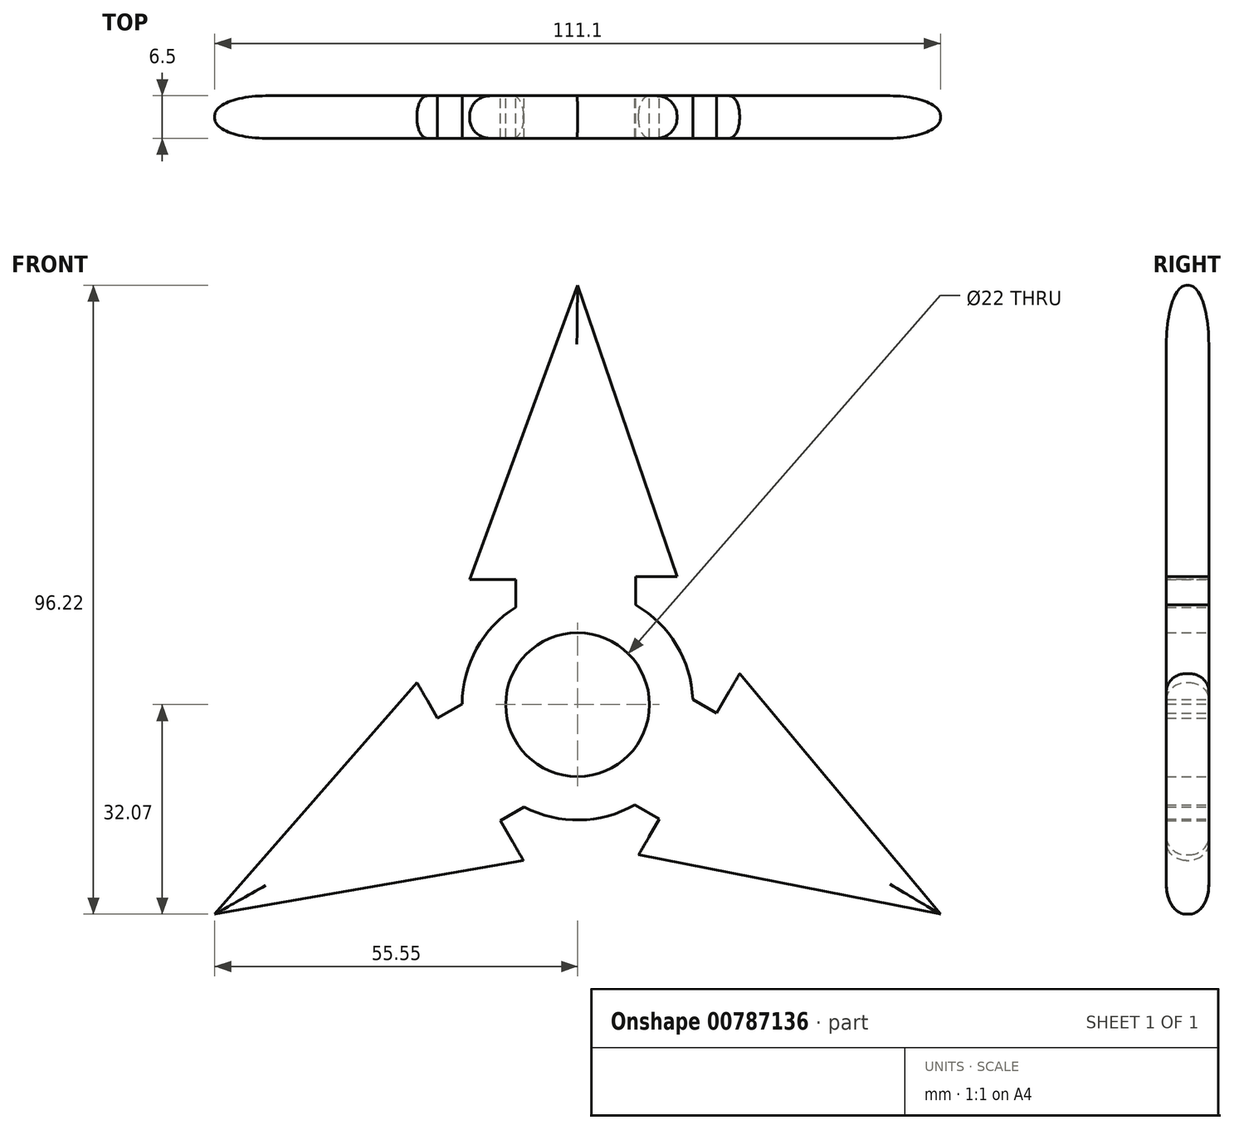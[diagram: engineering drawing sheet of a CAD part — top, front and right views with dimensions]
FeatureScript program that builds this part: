
annotation { "Feature Type Name" : "Feature", "Feature Type Description" : "" }
export const myFeature = defineFeature(function(context is Context, id is Id, definition is map)
    precondition{}
    {
        {
            var Q0;
            Q0=qCreatedBy(makeId("Front.planeOp"),FACE);
            var sketch = newSketch(context, id + "F0", { "sketchPlane" : qUnion([Q0])});
            skCircle(sketch, "E0", {"center": v(0, 0) * mm, "radius": 11 * mm});
            skCircle(sketch, "E1", {"center": v(0, 0) * mm, "radius": 17.66 * mm});
            skLineSegment(sketch, "E2", {"start": v(-16.51, 19.11) * mm, "end": v(0, 64.15) * mm});
            skLineSegment(sketch, "E3", {"start": v(0, 64.15) * mm, "end": v(15.22, 19.6) * mm});
            skLineSegment(sketch, "E4", {"start": v(8.92, 19.6) * mm, "end": v(15.22, 19.6) * mm});
            skLineSegment(sketch, "E5", {"start": v(-16.51, 19.11) * mm, "end": v(-9.49, 19.11) * mm});
            skLineSegment(sketch, "E6", {"start": v(-9.49, 19.11) * mm, "end": v(-9.49, 14.9) * mm});
            skLineSegment(sketch, "E7", {"start": v(8.92, 14.9) * mm, "end": v(8.92, 19.6) * mm});
            skLineSegment(sketch, "E8.1.0", {"start": v(-8.3, -23.85) * mm, "end": v(-55.55, -32.07) * mm});
            skLineSegment(sketch, "E8.1.1", {"start": v(-55.55, -32.07) * mm, "end": v(-24.58, 3.38) * mm});
            skLineSegment(sketch, "E8.1.2", {"start": v(-21.43, -2.07) * mm, "end": v(-24.58, 3.38) * mm});
            skLineSegment(sketch, "E8.1.3", {"start": v(-8.3, -23.85) * mm, "end": v(-11.8, -17.77) * mm});
            skLineSegment(sketch, "E8.1.4", {"start": v(-11.8, -17.77) * mm, "end": v(-8.16, -15.67) * mm});
            skLineSegment(sketch, "E8.1.5", {"start": v(-17.36, 0.28) * mm, "end": v(-21.43, -2.07) * mm});
            skLineSegment(sketch, "E8.2.0", {"start": v(24.8, 4.74) * mm, "end": v(55.55, -32.07) * mm});
            skLineSegment(sketch, "E8.2.1", {"start": v(55.55, -32.07) * mm, "end": v(9.36, -22.98) * mm});
            skLineSegment(sketch, "E8.2.2", {"start": v(12.5, -17.52) * mm, "end": v(9.36, -22.98) * mm});
            skLineSegment(sketch, "E8.2.3", {"start": v(24.8, 4.74) * mm, "end": v(21.3, -1.34) * mm});
            skLineSegment(sketch, "E8.2.4", {"start": v(21.3, -1.34) * mm, "end": v(17.65, 0.77) * mm});
            skLineSegment(sketch, "E8.2.5", {"start": v(8.44, -15.18) * mm, "end": v(12.5, -17.52) * mm});
            skSolve(sketch);
        }
        {
            var Q0;
            Q0 = qSketchRegion(id + "F0", true);
            extrude(context, id + "F1", {"entities" : qUnion([Q0]), "depth" : 6.5 * mm, "offsetDistance" : 25 * mm});
        }
        {
            var Q0;
            Q0=makeQuery(id+"F1.opExtrude","CAP_EDGE",EDGE,{"disambiguationData":[OSD([sQuery(id+"F0.wireOp",EDGE,"E2")])],"isStart":false});
            var Q1;
            Q1=makeQuery(id+"F1.opExtrude","CAP_EDGE",EDGE,{"disambiguationData":[OSD([sQuery(id+"F0.wireOp",EDGE,"E3")])],"isStart":false});
            var Q2;
            Q2=makeQuery(id+"F1.opExtrude","CAP_EDGE",EDGE,{"disambiguationData":[OSD([sQuery(id+"F0.wireOp",EDGE,"E8.2.0")])],"isStart":false});
            var Q3;
            Q3=makeQuery(id+"F1.opExtrude","CAP_EDGE",EDGE,{"disambiguationData":[OSD([sQuery(id+"F0.wireOp",EDGE,"E8.2.1")])],"isStart":false});
            var Q4;
            Q4=makeQuery(id+"F1.opExtrude","CAP_EDGE",EDGE,{"disambiguationData":[OSD([sQuery(id+"F0.wireOp",EDGE,"E8.1.0")])],"isStart":false});
            var Q5;
            Q5=makeQuery(id+"F1.opExtrude","CAP_EDGE",EDGE,{"disambiguationData":[OSD([sQuery(id+"F0.wireOp",EDGE,"E8.1.1")])],"isStart":false});
            fillet(context, id + "F2", {"entities" : qUnion([Q0, Q1, Q2, Q3, Q4, Q5]), "radius" : 3 * mm, "tangentPropagation" : true, "allowEdgeOverflow" : false});
        }
        {
            var Q0;
            Q0=makeQuery(id+"F1.opExtrude","CAP_EDGE",EDGE,{"disambiguationData":[OSD([sQuery(id+"F0.wireOp",EDGE,"E8.2.0")])],"isStart":true});
            var Q1;
            Q1=makeQuery(id+"F1.opExtrude","CAP_EDGE",EDGE,{"disambiguationData":[OSD([sQuery(id+"F0.wireOp",EDGE,"E8.1.0")])],"isStart":true});
            var Q2;
            Q2=makeQuery(id+"F1.opExtrude","CAP_EDGE",EDGE,{"disambiguationData":[OSD([sQuery(id+"F0.wireOp",EDGE,"E8.2.1")])],"isStart":true});
            var Q3;
            Q3=makeQuery(id+"F1.opExtrude","CAP_EDGE",EDGE,{"disambiguationData":[OSD([sQuery(id+"F0.wireOp",EDGE,"E8.1.1")])],"isStart":true});
            var Q4;
            Q4=makeQuery(id+"F1.opExtrude","CAP_EDGE",EDGE,{"disambiguationData":[OSD([sQuery(id+"F0.wireOp",EDGE,"E2")])],"isStart":true});
            var Q5;
            Q5=makeQuery(id+"F1.opExtrude","CAP_EDGE",EDGE,{"disambiguationData":[OSD([sQuery(id+"F0.wireOp",EDGE,"E3")])],"isStart":true});
            fillet(context, id + "F3", {"entities" : qUnion([Q0, Q1, Q2, Q3, Q4, Q5]), "radius" : 3 * mm, "tangentPropagation" : true, "allowEdgeOverflow" : false});
        }
    });
